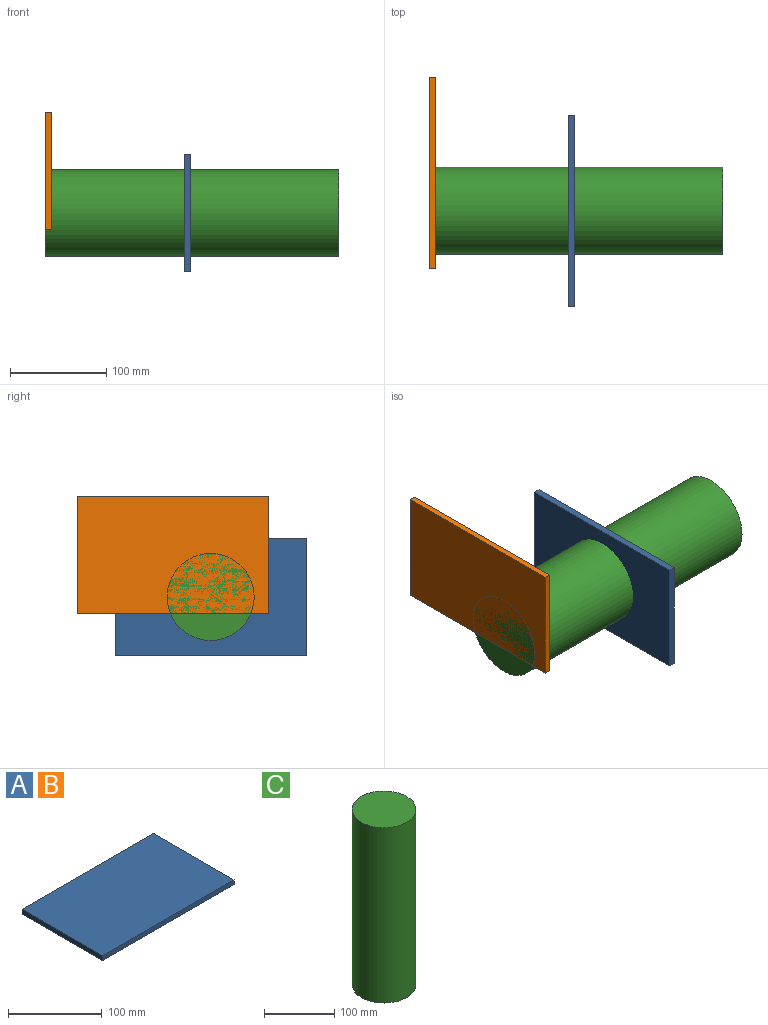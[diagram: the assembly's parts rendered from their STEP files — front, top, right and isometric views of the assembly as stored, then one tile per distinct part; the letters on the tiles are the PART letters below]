
ASSEMBLY  parts=3 mates=2
PART A: 6 faces, bbox 198.6x121.7x6.4 mm
  f0: plane 198.59x6.35mm, normal (0,1,0), area 1261mm2, adj f1,f3,f4,f5
  f1: plane 121.74x6.35mm, normal (-1,0,0), area 773.1mm2, adj f0,f2,f4,f5
  f2: plane 198.59x6.35mm, normal (0,-1,0), area 1261mm2, adj f1,f3,f4,f5
  f3: plane 121.74x6.35mm, normal (1,0,0), area 773.1mm2, adj f0,f2,f4,f5
  f4: plane 198.59x121.74mm, normal (0,0,1), area 24176.2mm2, adj f0,f1,f2,f3
  f5: plane 198.59x121.74mm, normal (0,0,-1), area 24176.2mm2, adj f0,f1,f2,f3
PART B: same geometry as A
PART C: 3 faces, bbox 90.5x90.5x304.8 mm
  f0: cylinder r=45.23mm len=304.8mm, axis (0,0,-1), area 86621.4mm2, adj f1,f2
  f1: plane 90.46x90.46mm, normal (0,0,1), area 6427mm2, adj f0
  f2: plane 90.46x90.46mm, normal (0,0,-1), area 6427mm2, adj f0
PLACE A rot(axis=(0.58,0.58,0.58),120deg) t=(-320.8,217.88,159.74)mm
PLACE B rot(axis=(0.58,-0.58,-0.58),120deg) t=(-459.09,354.19,203.33)mm
PLACE C rot(axis=(0,-1,0),90deg) t=(-160.64,263.36,148.95)mm
MATE cylindrical A.f4 <-> C.f0  axis (1,0,0) through (-314.45,266.66,145.07)mm
MATE planar B.f4 <-> C.f0  axis (-1,0,0) through (-465.44,305.41,188.65)mm
